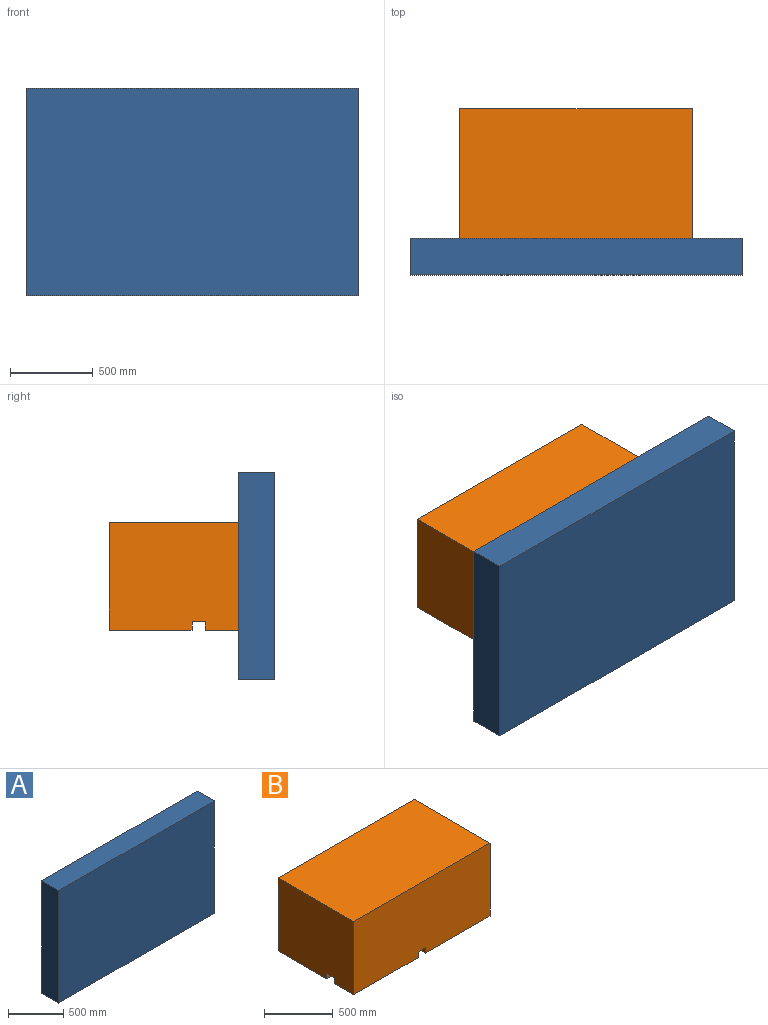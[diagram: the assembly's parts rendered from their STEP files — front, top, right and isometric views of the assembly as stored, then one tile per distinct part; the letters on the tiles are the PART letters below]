
ASSEMBLY  parts=2 mates=1
PART A: 6 faces, bbox 2000x220x1250 mm
  f0: plane 2000x220mm, normal (0,0,1), area 440000mm2, adj f1,f3,f4,f5
  f1: plane 1250x220mm, normal (-1,0,0), area 275000mm2, adj f0,f2,f4,f5
  f2: plane 2000x220mm, normal (0,0,-1), area 440000mm2, adj f1,f3,f4,f5
  f3: plane 1250x220mm, normal (1,0,0), area 275000mm2, adj f0,f2,f4,f5
  f4: plane 2000x1250mm, normal (0,-1,0), area 2500000mm2, adj f0,f1,f2,f3
  f5: plane 2000x1250mm, normal (0,1,0), area 2500000mm2, adj f0,f1,f2,f3
PART B: 18 faces, bbox 1400x780x650 mm
  f0: plane 660x200mm, normal (0,0,-1), area 132000mm2, adj f2,f4,f8,f16
  f1: plane 660x500mm, normal (0,0,-1), area 330000mm2, adj f3,f5,f8,f15
  f2: plane 1400x650mm, normal (0,-1,0), area 906000mm2, adj f0,f6,f7,f8,f9,f12,f16,f17
  f3: plane 1400x650mm, normal (0,1,0), area 906000mm2, adj f1,f6,f8,f9,f10,f12,f14,f15
  f4: plane 660x50mm, normal (0,1,0), area 33000mm2, adj f0,f8,f12,f16
  f5: plane 660x50mm, normal (0,-1,0), area 33000mm2, adj f1,f8,f12,f15
  f6: plane 780x650mm, normal (-1,0,0), area 503000mm2, adj f2,f3,f7,f9,f10,f11,f12,f13
  f7: plane 660x200mm, normal (0,0,-1), area 132000mm2, adj f2,f6,f11,f17
  f8: plane 780x650mm, normal (1,0,0), area 503000mm2, adj f0,f1,f2,f3,f4,f5,f9,f12
  f9: plane 1400x780mm, normal (0,0,1), area 1092000mm2, adj f2,f3,f6,f8
  f10: plane 660x500mm, normal (0,0,-1), area 330000mm2, adj f3,f6,f13,f14
  f11: plane 660x50mm, normal (0,1,0), area 33000mm2, adj f6,f7,f12,f17
  f12: plane 1400x780mm, normal (0,0,-1), area 168000mm2, adj f2,f3,f4,f5,f6,f8,f11,f13
  f13: plane 660x50mm, normal (0,-1,0), area 33000mm2, adj f6,f10,f12,f14
  f14: plane 500x50mm, normal (1,0,0), area 25000mm2, adj f3,f10,f12,f13
  f15: plane 500x50mm, normal (-1,0,0), area 25000mm2, adj f1,f3,f5,f12
  f16: plane 200x50mm, normal (-1,0,0), area 10000mm2, adj f0,f2,f4,f12
  f17: plane 200x50mm, normal (1,0,0), area 10000mm2, adj f2,f7,f11,f12
PLACE A t=(0,-780,1.32)mm
PLACE B at identity fixed
MATE fastened B.f2 <-> A.f5  axis (0,-1,0) through (0,-780,1.32)mm
